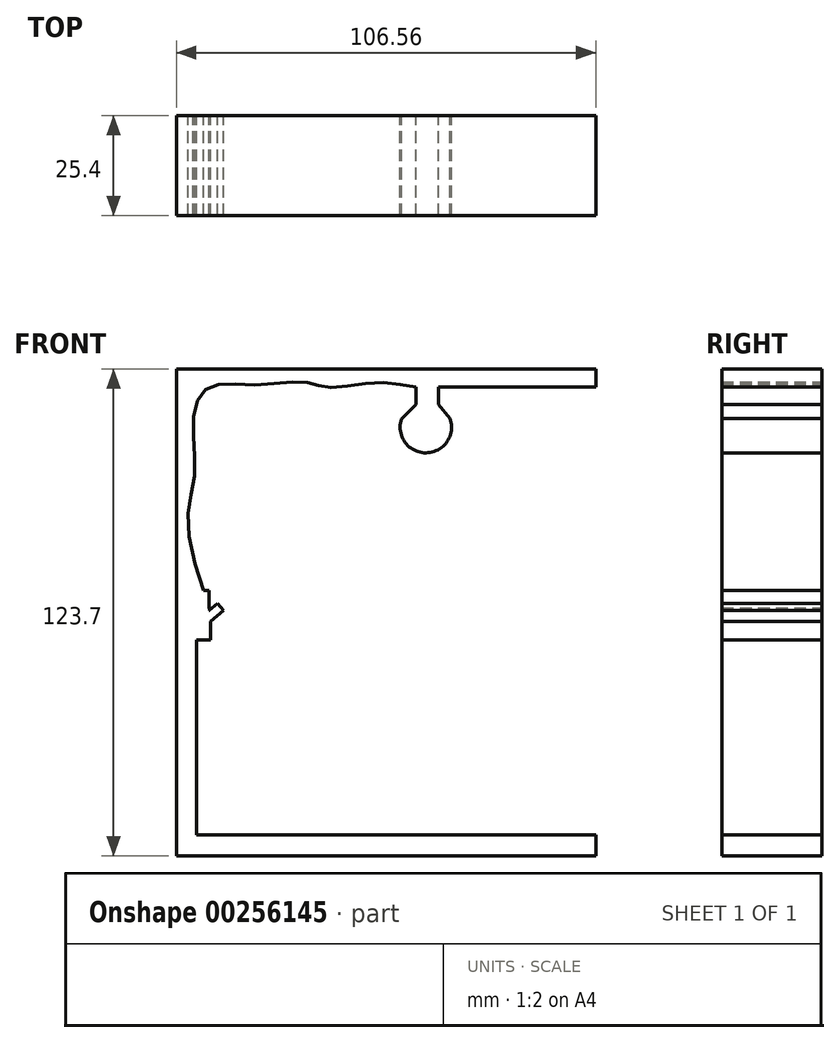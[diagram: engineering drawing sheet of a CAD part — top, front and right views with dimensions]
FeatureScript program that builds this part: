
annotation { "Feature Type Name" : "Feature", "Feature Type Description" : "" }
export const myFeature = defineFeature(function(context is Context, id is Id, definition is map)
    precondition{}
    {
        {
            var Q0;
            Q0=qCreatedBy(makeId("Front.planeOp"),FACE);
            var sketch = newSketch(context, id + "F0", { "sketchPlane" : qUnion([Q0])});
            skArc(sketch, "E0", {"start": v(-5.9, 54.57) * mm, "mid": v(0.4, 46) * mm, "end": v(6.45, 54.75) * mm});
            skLineSegment(sketch, "E1", {"start": v(-5.9, 54.57) * mm, "end": v(-2.21, 58.26) * mm});
            skLineSegment(sketch, "E2", {"start": v(-2.21, 58.26) * mm, "end": v(-2.21, 62.68) * mm});
            skLineSegment(sketch, "E3", {"start": v(6.45, 54.75) * mm, "end": v(3.5, 58.26) * mm});
            skLineSegment(sketch, "E4", {"start": v(3.5, 58.26) * mm, "end": v(3.5, 62.68) * mm});
            skLineSegment(sketch, "E5", {"start": v(3.5, 62.68) * mm, "end": v(43.5, 62.68) * mm});
            skLineSegment(sketch, "E6", {"start": v(43.5, 62.68) * mm, "end": v(43.5, 67.29) * mm});
            skLineSegment(sketch, "E7", {"start": v(43.5, 67.29) * mm, "end": v(-63.05, 67.29) * mm});
            skLineSegment(sketch, "E8", {"start": v(-63.05, 67.29) * mm, "end": v(-63.05, -56.41) * mm});
            skLineSegment(sketch, "E9", {"start": v(-63.05, -56.41) * mm, "end": v(43.5, -56.41) * mm});
            skLineSegment(sketch, "E10", {"start": v(43.5, -56.41) * mm, "end": v(43.5, -51.07) * mm});
            skLineSegment(sketch, "E11", {"start": v(43.5, -51.07) * mm, "end": v(-57.89, -51.07) * mm});
            skLineSegment(sketch, "E12", {"start": v(-57.89, -51.07) * mm, "end": v(-57.89, -1.47) * mm});
            skLineSegment(sketch, "E13", {"start": v(-57.89, -1.47) * mm, "end": v(-54.38, -1.47) * mm});
            skLineSegment(sketch, "E14", {"start": v(-54.38, -1.47) * mm, "end": v(-54.38, 3.13) * mm});
            skLineSegment(sketch, "E15", {"start": v(-54.38, 3.13) * mm, "end": v(-51.07, 5.9) * mm});
            skLineSegment(sketch, "E16", {"start": v(-51.07, 5.9) * mm, "end": v(-52.56, 7.7) * mm});
            skLineSegment(sketch, "E17", {"start": v(-52.56, 7.7) * mm, "end": v(-54.72, 5.9) * mm});
            skLineSegment(sketch, "E18", {"start": v(-54.72, 5.9) * mm, "end": v(-54.72, 11.06) * mm});
            skPoint(sketch, "E19.end.orphan", {"position": v(-57.89, 11.06) * mm});
            skFitSpline(sketch, "E20", {"points": [v(-54.72, 5.9) * mm, v(-59.9, 24.85) * mm, v(-58.41, 40.78) * mm, v(-58.58, 56.22) * mm, v(-54.38, 62.8) * mm, v(-42.81, 63.28) * mm, v(-30.16, 63.94) * mm, v(-24.74, 62.63) * mm, v(-13.08, 63.78) * mm, v(-2.21, 62.68) * mm, v(3.5, 62.68) * mm, v(3.5, 65.58) * mm, v(-2.21, 65.58) * mm, v(-12.75, 65.58) * mm, v(-22.28, 64.27) * mm, v(-31.15, 66.08) * mm, v(-42.65, 65.25) * mm, v(-54.38, 64.93) * mm, v(-58.58, 62.68) * mm, v(-61.37, 53.76) * mm, v(-60.71, 35.03) * mm, v(-61.53, 24.69) * mm, v(-60.06, 14.67) * mm, v(-54.72, 5.9) * mm]});
            skLineSegment(sketch, "E21", {"start": v(-54.72, 11.06) * mm, "end": v(-56.12, 11.06) * mm});
            skSolve(sketch);
        }
        {
            var Q0;
            Q0 = qSketchRegion(id + "F0", true);
            extrude(context, id + "F1", {"entities" : qUnion([Q0]), "depth" : 25.4 * mm});
        }
    });
